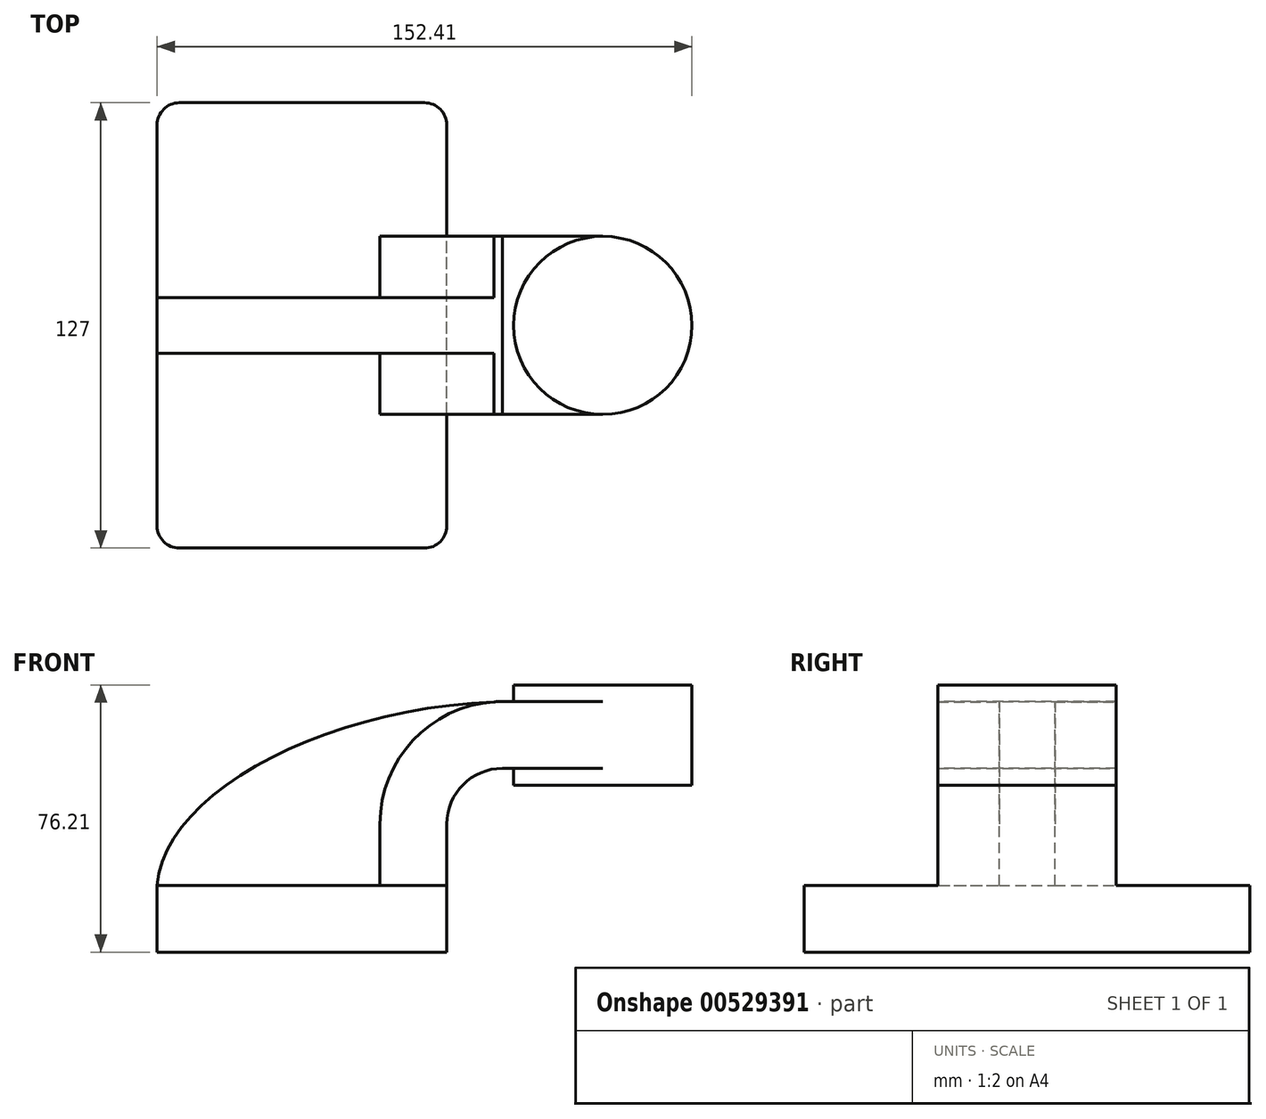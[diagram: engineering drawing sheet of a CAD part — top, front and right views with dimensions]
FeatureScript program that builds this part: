
annotation { "Feature Type Name" : "Feature", "Feature Type Description" : "" }
export const myFeature = defineFeature(function(context is Context, id is Id, definition is map)
    precondition{}
    {
        {
            var Q0;
            Q0=qCreatedBy(makeId("Front.planeOp"),FACE);
            var sketch = newSketch(context, id + "F0", { "sketchPlane" : qUnion([Q0])});
            skLineSegment(sketch, "E0.bottom", {"start": v(-41.28, 9.52) * mm, "end": v(41.28, 9.53) * mm});
            skLineSegment(sketch, "E0.top", {"start": v(-41.28, -9.53) * mm, "end": v(41.28, -9.53) * mm});
            skLineSegment(sketch, "E0.left", {"start": v(-41.28, 9.52) * mm, "end": v(-41.27, -9.53) * mm});
            skLineSegment(sketch, "E0.right", {"start": v(41.28, 9.53) * mm, "end": v(41.28, -9.52) * mm});
            skPoint(sketch, "E0.middle", {"position": v(0, 0) * mm});
            skLineSegment(sketch, "E1.bottom", {"start": v(111.12, 66.68) * mm, "end": v(60.32, 66.68) * mm});
            skLineSegment(sketch, "E1.top", {"start": v(111.12, 38.1) * mm, "end": v(60.32, 38.1) * mm});
            skLineSegment(sketch, "E1.left", {"start": v(111.12, 66.68) * mm, "end": v(111.12, 38.1) * mm});
            skLineSegment(sketch, "E1.right", {"start": v(60.32, 66.68) * mm, "end": v(60.32, 38.1) * mm});
            skPoint(sketch, "E1.middle", {"position": v(85.72, 52.39) * mm});
            skLineSegment(sketch, "E2", {"start": v(41.27, 9.53) * mm, "end": v(41.27, 27) * mm});
            skArc(sketch, "E3", {"start": v(41.27, 27) * mm, "mid": v(45.92, 38.23) * mm, "end": v(57.15, 42.88) * mm});
            skLineSegment(sketch, "E4", {"start": v(57.15, 42.88) * mm, "end": v(85.72, 42.88) * mm});
            skLineSegment(sketch, "E5.0", {"start": v(57.15, 61.93) * mm, "end": v(85.72, 61.93) * mm});
            skArc(sketch, "E5.1", {"start": v(22.22, 27) * mm, "mid": v(32.45, 51.7) * mm, "end": v(57.15, 61.93) * mm});
            skLineSegment(sketch, "E5.2", {"start": v(22.22, 9.53) * mm, "end": v(22.22, 27) * mm});
            skLineSegment(sketch, "E6", {"start": v(85.72, 66.68) * mm, "end": v(85.72, 38.1) * mm});
            skFitSpline(sketch, "E7", {"points": [v(-41.28, 9.52) * mm, v(57.15, 61.93) * mm], "startDerivative": vector(5.7, 79.65) * mm, "endDerivative": vector(150.27, 4.07) * mm});
            skSolve(sketch);
        }
        {
            var Q0;
            Q0=makeQuery(id+"F0.imprint","IMPRINT",FACE,{"disambiguationData":[TD([[makeQuery(id+"F0.imprint","IMPRINT",EDGE,{"derivedFrom":sQuery(id+"F0.wireOp",EDGE,"E0.top")}),1.0]])]});
            extrude(context, id + "F1", {"entities" : qUnion([Q0]), "endBound" : BoundingType.SYMMETRIC, "depth" : 127 * mm, "offsetDistance" : 25.4 * mm});
        }
        {
            var Q0;
            {var subQ1=sQuery(id+"F0.wireOp",EDGE,"E2");Q0=makeQuery(id+"F0.imprint","IMPRINT",FACE,{"disambiguationData":[TD([[makeQuery(id+"F0.imprint","IMPRINT",EDGE,{"derivedFrom":subQ1}),1.0]])]});}
            var Q1;
            {var subQ0=sQuery(id+"F0.wireOp",EDGE,"E5.0");var subQ1=sQuery(id+"F0.wireOp",EDGE,"E1.right");var subQ2=makeQuery(id+"F0.imprint","INTERSECT",VERTEX,{"derivedFrom":[subQ1,subQ0]});Q1=makeQuery(id+"F0.imprint","IMPRINT",FACE,{"disambiguationData":[TD([[makeQuery(id+"F0.imprint","IMPRINT",EDGE,{"disambiguationData":[TD([[subQ2,-1.0]])],"derivedFrom":subQ1}),1.0]])]});}
            extrude(context, id + "F2", {"entities" : qUnion([Q0, Q1]), "operationType" : NewBodyOperationType.ADD, "endBound" : BoundingType.SYMMETRIC, "depth" : 50.8 * mm, "offsetDistance" : 25.4 * mm});
        }
        {
            var Q0;
            {var subQ3=sQuery(id+"F0.wireOp",EDGE,"E5.2");Q0=makeQuery(id+"F0.imprint","IMPRINT",FACE,{"disambiguationData":[TD([[makeQuery(id+"F0.imprint","IMPRINT",EDGE,{"derivedFrom":subQ3}),1.0]])]});}
            extrude(context, id + "F3", {"entities" : qUnion([Q0]), "operationType" : NewBodyOperationType.ADD, "endBound" : BoundingType.SYMMETRIC, "depth" : 15.88 * mm, "offsetDistance" : 25.4 * mm});
        }
        {
            var Q0;
            {var subQ0=sQuery(id+"F0.wireOp",EDGE,"E1.left");Q0=makeQuery(id+"F0.imprint","IMPRINT",FACE,{"disambiguationData":[TD([[makeQuery(id+"F0.imprint","IMPRINT",EDGE,{"derivedFrom":subQ0}),-1.0]])]});}
            var Q1;
            Q1=sQuery(id+"F0.wireOp",EDGE,"E6");
            revolve(context, id + "F4", {"operationType" : NewBodyOperationType.ADD, "entities" : qUnion([Q0]), "axis" : qUnion([Q1]), "revolveType" : RevolveType.FULL});
        }
        {
            var Q0;
            Q0=makeQuery(id+"F1.opExtrude","CAP_EDGE",EDGE,{"disambiguationData":[OSD([sQuery(id+"F0.wireOp",EDGE,"E0.right")])],"isStart":false});
            var Q1;
            Q1=makeQuery(id+"F1.opExtrude","CAP_EDGE",EDGE,{"disambiguationData":[OSD([sQuery(id+"F0.wireOp",EDGE,"E0.left")])],"isStart":false});
            var Q2;
            Q2=makeQuery(id+"F1.opExtrude","CAP_EDGE",EDGE,{"disambiguationData":[OSD([sQuery(id+"F0.wireOp",EDGE,"E0.right")])],"isStart":true});
            var Q3;
            Q3=makeQuery(id+"F1.opExtrude","CAP_EDGE",EDGE,{"disambiguationData":[OSD([sQuery(id+"F0.wireOp",EDGE,"E0.left")])],"isStart":true});
            fillet(context, id + "F5", {"entities" : qUnion([Q0, Q1, Q2, Q3]), "radius" : 6.35 * mm, "tangentPropagation" : true, "allowEdgeOverflow" : false});
        }
    });
